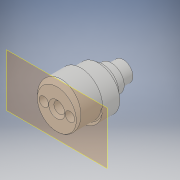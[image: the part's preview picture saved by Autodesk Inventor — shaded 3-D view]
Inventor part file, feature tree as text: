
AUTODESK INVENTOR PART (.ipt)
format: ipt  version: 2019.4 (Build 234330000, 330)  size: 333,824 bytes
history: native  units: mm
features: sketch x18, extrude x15, fillet x4, projected_geometry x4, chamfer x2, hole x2, revolve x1, plane x1, pattern_circular x1
ambient origin geometry x8: Origin, YZ Plane, XZ Plane, XY Plane, X Axis, Y Axis, Z Axis, Center Point
bodies: Solid1 (feature_tree)
feature tree (48):
  extrude  "Extrusion1"  Depth=1.0mm
  revolve  "Revolution1"  [1 undecoded]
  extrude  "Extrusion2"  Depth=4.0mm
  chamfer  "Chamfer1"  Distance=8.0mm
  extrude  "Extrusion6"  Depth=1.0mm TaperAngle=45.0deg
  extrude  "Extrusion7"  Depth=2.0mm TaperAngle=0.0deg
  extrude  "Extrusion8"  Depth=4.0mm TaperAngle=0.0deg
  extrude  "Extrusion9"  Depth=8.0mm
  hole  "Hole1"  [1 undecoded]
  extrude  "Extrusion10"  Depth=1.5mm TaperAngle=0.0deg
  extrude  "Extrusion11"  TaperAngle=0.0deg  [1 undecoded]
  fillet  "Fillet7"  Radius=20.0mm
  extrude  "Extrusion13"  Depth=24.0mm
  extrude  "Extrusion14"  Depth=3.0mm TaperAngle=0.0deg
  fillet  "Fillet9"  Radius=2.0mm
  extrude  "Extrusion15"  Depth=10.1mm
  extrude  "Extrusion16"  Depth=2.0mm
  extrude  "Extrusion17"  Depth=7.0mm TaperAngle=0.0deg
  fillet  "Fillet10"  Radius=6.1mm
  fillet  "Fillet11"  Radius=3.0mm
  plane  "Work Plane1"
  extrude  "Extrusion18"  Depth=7.0mm TaperAngle=0.0deg
  extrude  "Extrusion19"  Depth=1.0mm
  hole  "Hole2"  [1 undecoded]
  pattern_circular  "Circular Pattern1"  [2 undecoded]
  chamfer  "Chamfer4"  Distance=10.0mm
  sketch  "Sketch1"  dims[d0=3.0mm d1=1.0mm]
  sketch  "Sketch2"  dims[d2=19.9mm d3=14.0mm d4=0.0mm]
  sketch  "Sketch3"  dims[d5=3.0mm d6=4.0mm]
  projected_geometry  "Projected Loop1"
  sketch  "Sketch7"  dims[d7=4.0mm]
  sketch  "Sketch8"  dims[d8=90.0deg]
  sketch  "Sketch9"  dims[d10=19.9mm d11=8.0mm d12=0.0mm]
  sketch  "Sketch10"  dims[d13=1.0mm d18=0.5mm d19=2.0mm d20=45.0deg]
  projected_geometry  "Projected Loop2"
  sketch  "Sketch11"  dims[d33=15.0mm d34=2.0mm d35=0.0mm]
  sketch  "Sketch12"  dims[d36=11.92mm d37=4.0mm d38=0.0mm]
  sketch  "Sketch13"  dims[d39=34.0mm d40=8.0mm]
  sketch  "Sketch16"  dims[d41=2.0mm d42=0.0mm d43=8.0mm]
  projected_geometry  "Projected Loop3"
  sketch  "Sketch17"  dims[d44=8.0mm d45=1.5mm d46=0.0mm]
  sketch  "Sketch18"  dims[d47=3.1mm d48=5.2mm d49=6.5mm d50=2.0mm d51=90.0deg d52=10.0mm d53=0.0mm d58=0.0mm d59=20.0mm]
  sketch  "Sketch19"  dims[d60=3.0mm d61=0.0mm d63=24.0mm]
  projected_geometry  "Projected Loop4"
  sketch  "Sketch20"  dims[d64=15.0mm d65=3.0mm d66=0.0mm d68=2.0mm]
  sketch  "Sketch21"  dims[d74=3.0mm d75=0.0mm d76=10.1mm]
  sketch  "Sketch22"  dims[d77=3.0mm d78=0.0mm d79=2.0mm]
  sketch  "Sketch23"  dims[d80=9.0mm d81=5.5mm d82=0.0mm d83=6.1mm d84=3.0mm d85=0.0mm d86=2.5mm d87=0.0mm d88=1.0mm d89=1.0mm d90=11.0mm d91=10.0mm d92=0.0mm d93=5.08mm d94=6.0mm d95=0.0mm d96=3.0mm d97=6.0mm d98=3.88mm d99=4.6mm d100=4.34mm d101=2.0mm d102=1.22173mm d103=7.0mm d104=0.0mm d105=20.0mm d106=360.0deg d108=1.2mm d109=2.0mm d110=45.0deg]
note: 6 required parameter values undecoded (feature->parameter linkage not recoverable at this tier; creation-order binding heuristic only, values carry confidence <= 0.55)